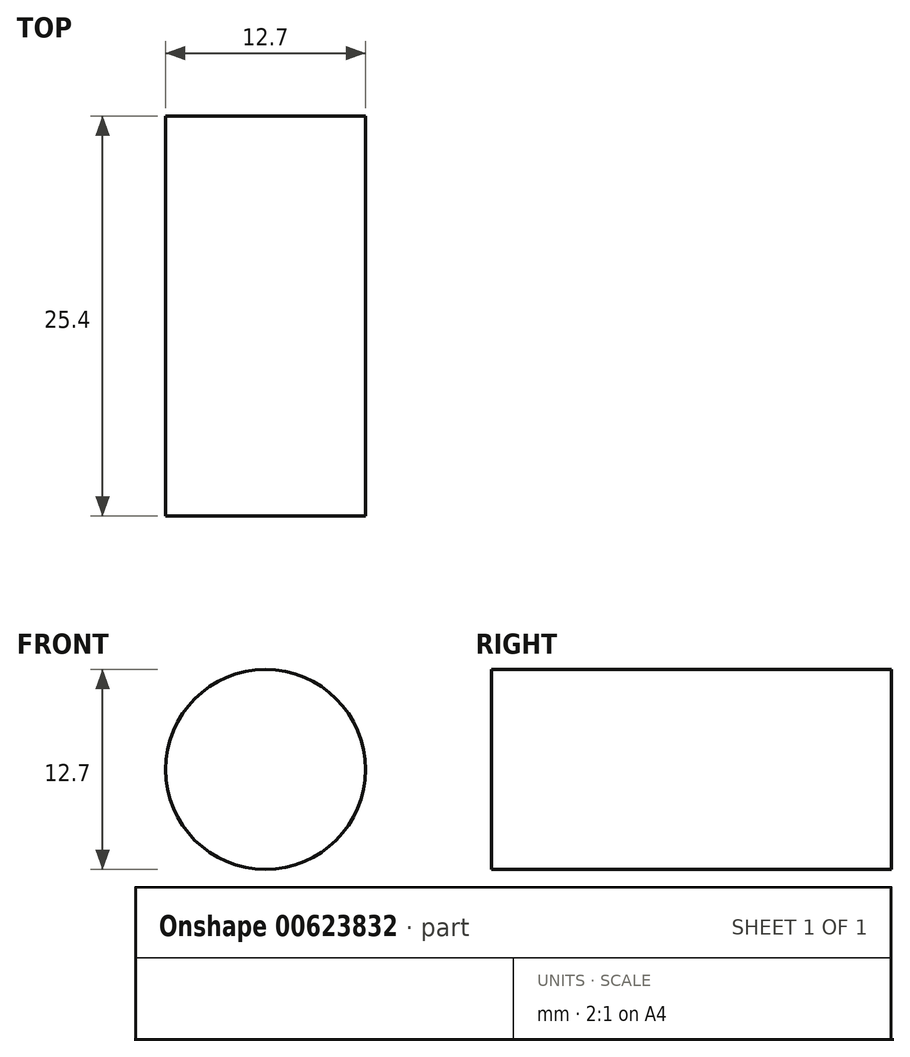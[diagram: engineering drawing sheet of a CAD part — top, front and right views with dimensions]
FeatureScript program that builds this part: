
annotation { "Feature Type Name" : "Feature", "Feature Type Description" : "" }
export const myFeature = defineFeature(function(context is Context, id is Id, definition is map)
    precondition{}
    {
        {
            var Q0;
            Q0=qCreatedBy(makeId("Front.planeOp"),FACE);
            var sketch = newSketch(context, id + "F0", { "sketchPlane" : qUnion([Q0])});
            skCircle(sketch, "E0", {"center": v(-62.54, 50.5) * mm, "radius": 6.35 * mm});
            skSolve(sketch);
        }
        {
            var Q0;
            Q0=makeQuery(id+"F0.imprint","IMPRINT",FACE,{"disambiguationData":[TD([[makeQuery(id+"F0.imprint","IMPRINT",EDGE,{"derivedFrom":sQuery(id+"F0.wireOp",EDGE,"E0")}),1.0]])]});
            extrude(context, id + "F1", {"entities" : qUnion([Q0]), "depth" : 25.4 * mm, "offsetDistance" : 25.4 * mm});
        }
    });
